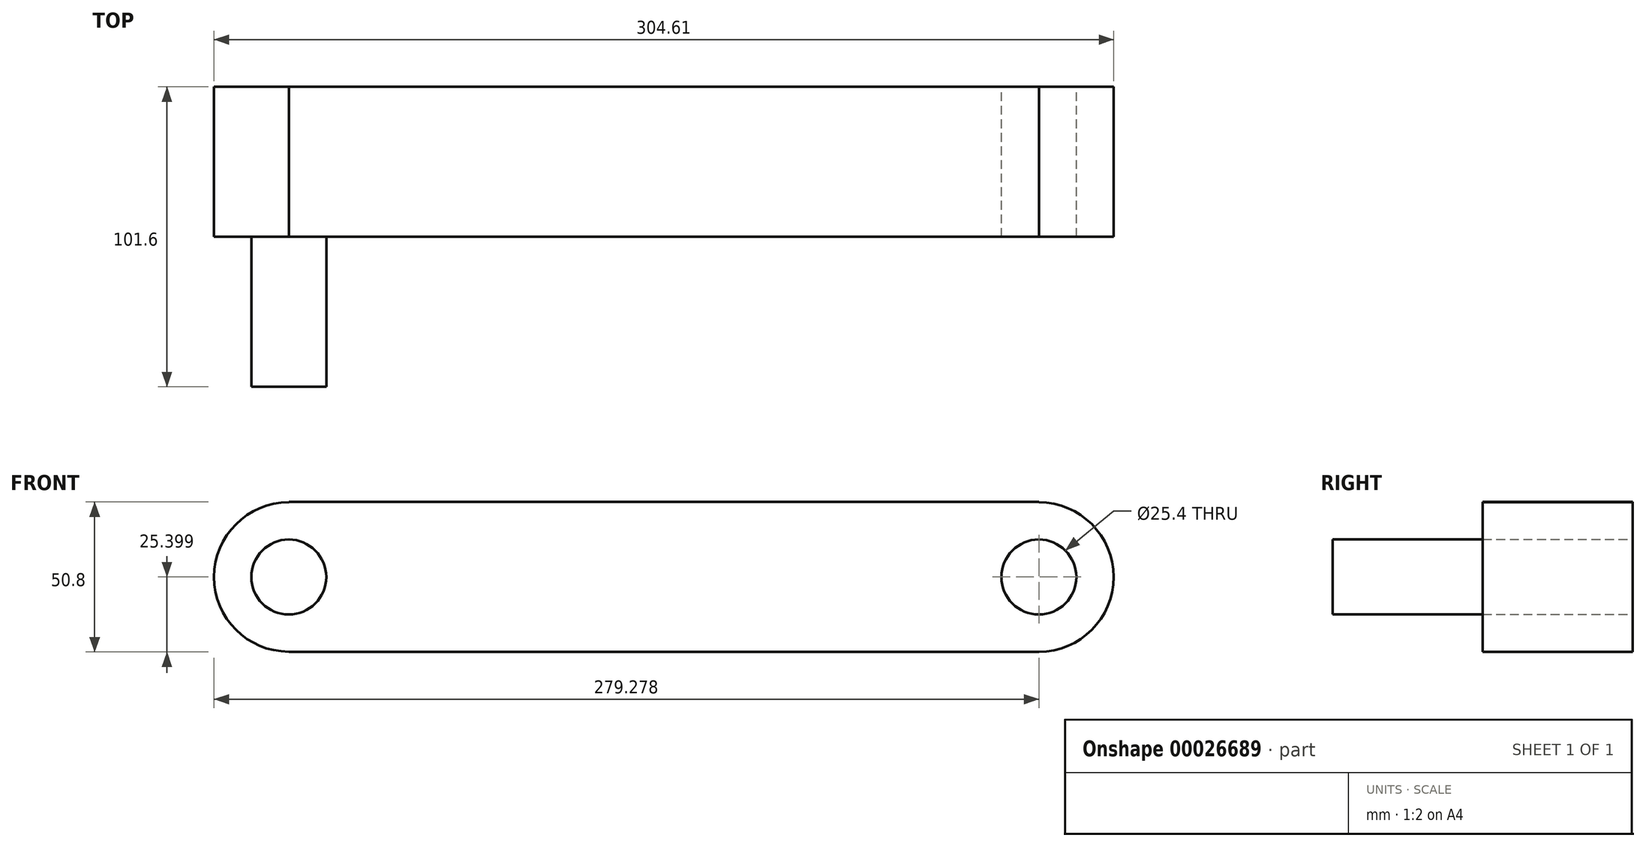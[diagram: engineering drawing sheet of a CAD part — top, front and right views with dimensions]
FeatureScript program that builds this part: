
annotation { "Feature Type Name" : "Feature", "Feature Type Description" : "" }
export const myFeature = defineFeature(function(context is Context, id is Id, definition is map)
    precondition{}
    {
        {
            var Q0;
            Q0=qCreatedBy(makeId("Front.planeOp"),FACE);
            var sketch = newSketch(context, id + "F0", { "sketchPlane" : qUnion([Q0])});
            skLineSegment(sketch, "E0.bottom", {"start": v(-98.84, 26.22) * mm, "end": v(155.16, 26.22) * mm});
            skLineSegment(sketch, "E0.top", {"start": v(-98.84, -24.58) * mm, "end": v(155.16, -24.58) * mm});
            skLineSegment(sketch, "E0.left", {"start": v(-98.84, 26.22) * mm, "end": v(-98.84, 13.52) * mm});
            skLineSegment(sketch, "E0.right", {"start": v(155.16, 26.22) * mm, "end": v(155.16, 13.52) * mm});
            skCircle(sketch, "E1", {"center": v(155.16, 0.82) * mm, "radius": 25.33 * mm});
            skCircle(sketch, "E2", {"center": v(-98.84, 0.82) * mm, "radius": 25.28 * mm});
            skCircle(sketch, "E3", {"center": v(155.16, 0.82) * mm, "radius": 12.7 * mm});
            skLineSegment(sketch, "E4.trimOffspring", {"start": v(155.16, -11.88) * mm, "end": v(155.16, -24.58) * mm});
            skCircle(sketch, "E5", {"center": v(-98.84, 0.82) * mm, "radius": 12.7 * mm});
            skLineSegment(sketch, "E6.trimOffspring", {"start": v(-98.84, -11.88) * mm, "end": v(-98.84, -24.58) * mm});
            skSolve(sketch);
        }
        {
            var Q0;
            Q0=makeQuery(id+"F0.imprint","IMPRINT",FACE,{"disambiguationData":[TD([[makeQuery(id+"F0.imprint","IMPRINT",EDGE,{"derivedFrom":sQuery(id+"F0.wireOp",EDGE,"E0.bottom")}),-1.0]])]});
            extrude(context, id + "F1", {"entities" : qUnion([Q0]), "depth" : 50.8 * mm});
        }
        {
            var Q0;
            Q0 = qSketchRegion(id + "F0", true);
            extrude(context, id + "F2", {"entities" : qUnion([Q0]), "operationType" : NewBodyOperationType.ADD, "depth" : 50.8 * mm});
        }
        {
            var Q0;
            Q0 = qSketchRegion(id + "F0", true);
            extrude(context, id + "F3", {"entities" : qUnion([Q0]), "operationType" : NewBodyOperationType.ADD, "depth" : 25.4 * mm});
        }
        {
            var Q0;
            {var subQ0=sQuery(id+"F0.wireOp",EDGE,"E5");var subQ2=makeQuery(id+"F0.imprint","INTERSECT",VERTEX,{"derivedFrom":[sQuery(id+"F0.wireOp",EDGE,"E0.left"),subQ0]});Q0=makeQuery(id+"F0.imprint","IMPRINT",FACE,{"disambiguationData":[TD([[makeQuery(id+"F0.imprint","IMPRINT",EDGE,{"disambiguationData":[TD([[subQ2,-1.0]])],"derivedFrom":subQ0}),1.0]])]});}
            extrude(context, id + "F4", {"entities" : qUnion([Q0]), "operationType" : NewBodyOperationType.ADD, "depth" : 101.6 * mm});
        }
    });
